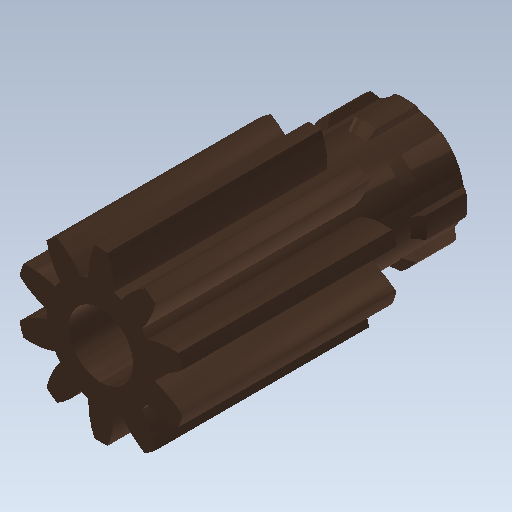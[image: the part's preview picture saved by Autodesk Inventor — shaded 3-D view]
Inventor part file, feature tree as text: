
AUTODESK INVENTOR PART (.ipt)
format: ipt  version: 2020 (Build 240168000, 168)  size: 284,160 bytes
history: native  units: mm (DEFAULTED — no unit token found)
features: sketch x5, extrude x4, plane x3, other x3, chamfer x2, pattern_circular x1, projected_geometry x1
ambient origin geometry x8: Origin, YZ Plane, XZ Plane, XY Plane, X Axis, Y Axis, Z Axis, Center Point
bodies: Solid1 (feature_tree)
feature tree (19):
  extrude  "Extrusion1"  Depth=4.0mm TaperAngle=0.0deg
  plane  "Work Plane2"
  plane  "Work Plane8"
  plane  "Work Plane9"
  other  "Цилиндрическое зубчатое зацепление"
  extrude  "Выдавливание2"  Depth=10.0mm TaperAngle=0.0deg
  extrude  "Выдавливание3"  Depth=1.0mm
  chamfer  "Фаска1"  Distance=3.141593mm
  chamfer  "Фаска2"  [1 undecoded]
  pattern_circular  "Круговой массив1"  [2 undecoded]
  extrude  "Выдавливание4"  Depth=1.0mm
  sketch  "Sketch1"  dims[d0=3.135mm d1=4.0mm d2=0.0mm]
  sketch  "Sketch2"  dims[d3=2.5mm d4=10.0mm d5=0.0mm d16=6.0mm d17=0.0mm d34=3.141593mm d39=0.0mm d41=0.0mm d43=6.0mm d46=6.0mm d47=0.0mm d48=0.0mm d49=2.0mm d50=1.8mm d51=0.0mm d52=0.15mm d53=3.490659mm d54=1.0mm d55=0.0mm d56=0.15mm d57=2.0mm d58=45.0deg d59=0.15mm d60=0.1mm d61=45.0deg d62=80.0mm d63=360.0deg d65=1.2mm d66=6.75mm d67=0.0mm]
  other  "Srf1"
  sketch  "Эскиз3"
  sketch  "Эскиз4"
  projected_geometry  "Спроецированная петля1"
  sketch  "Эскиз5"
  other  "Средний диаметр"
note: 3 required parameter values undecoded (feature->parameter linkage not recoverable at this tier; creation-order binding heuristic only, values carry confidence <= 0.55)
